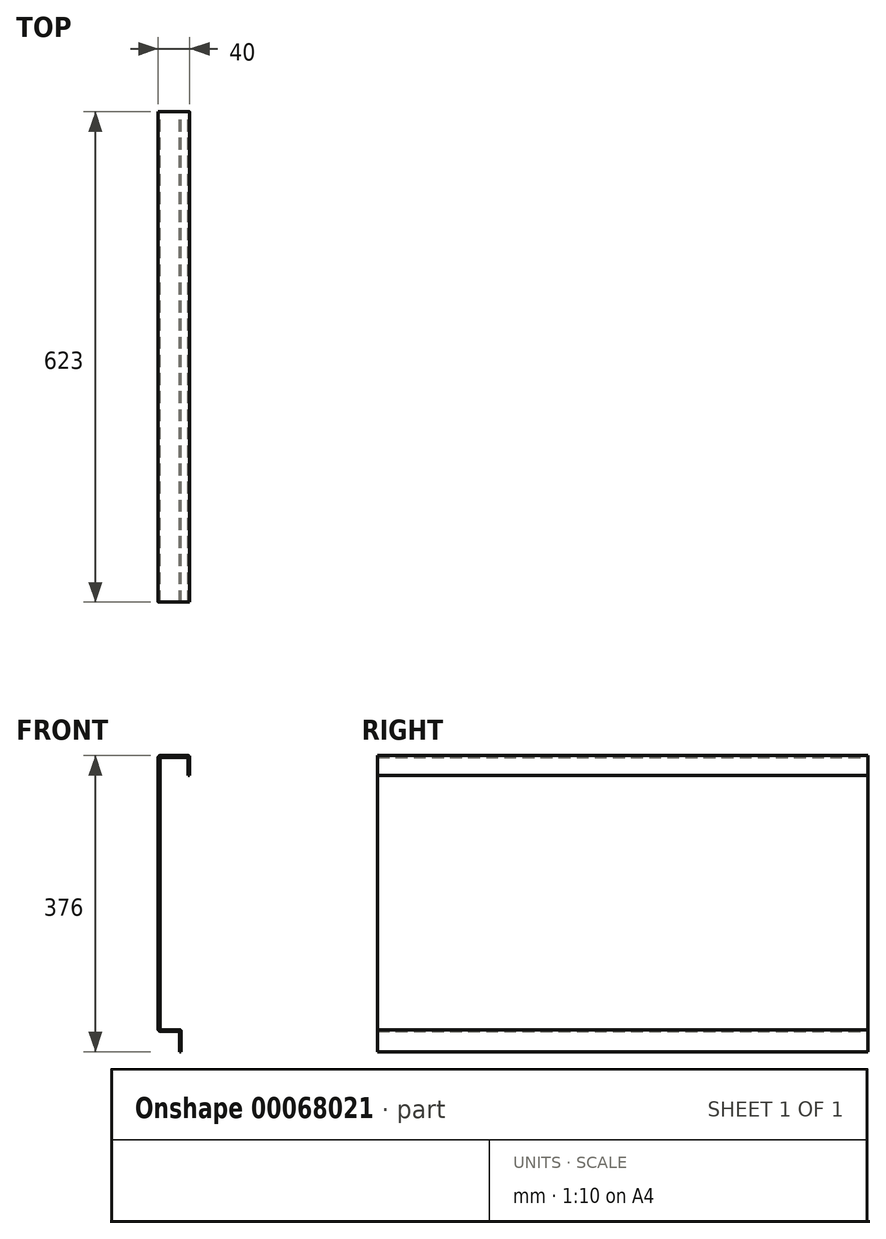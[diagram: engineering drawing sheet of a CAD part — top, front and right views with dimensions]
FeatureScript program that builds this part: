
annotation { "Feature Type Name" : "Feature", "Feature Type Description" : "" }
export const myFeature = defineFeature(function(context is Context, id is Id, definition is map)
    precondition{}
    {
        {
            var Q0;
            Q0=qCreatedBy(makeId("Front.planeOp"),FACE);
            var sketch = newSketch(context, id + "F0", { "sketchPlane" : qUnion([Q0])});
            skLineSegment(sketch, "E0", {"start": v(0, 0) * mm, "end": v(0, -350) * mm});
            skLineSegment(sketch, "E1", {"start": v(0, -350) * mm, "end": v(27, -350) * mm});
            skLineSegment(sketch, "E2", {"start": v(27, -350) * mm, "end": v(27, -376) * mm});
            skLineSegment(sketch, "E3", {"start": v(0, 0) * mm, "end": v(40, 0) * mm});
            skLineSegment(sketch, "E4", {"start": v(40, 0) * mm, "end": v(40, -25) * mm});
            skLineSegment(sketch, "E5.0", {"start": v(38, -2) * mm, "end": v(38, -25) * mm});
            skLineSegment(sketch, "E5.1", {"start": v(29, -348) * mm, "end": v(29, -376) * mm});
            skLineSegment(sketch, "E5.2", {"start": v(2, -348) * mm, "end": v(29, -348) * mm});
            skLineSegment(sketch, "E5.3", {"start": v(2, -2) * mm, "end": v(2, -348) * mm});
            skLineSegment(sketch, "E5.4", {"start": v(2, -2) * mm, "end": v(38, -2) * mm});
            skLineSegment(sketch, "E6", {"start": v(38, -25) * mm, "end": v(40, -25) * mm});
            skLineSegment(sketch, "E7", {"start": v(27, -376) * mm, "end": v(29, -376) * mm});
            skSolve(sketch);
        }
        {
            var Q0;
            Q0=qCreatedBy(makeId("Top.planeOp"),FACE);
            var sketch = newSketch(context, id + "F1", { "sketchPlane" : qUnion([Q0])});
            skLineSegment(sketch, "E8", {"start": v(0, 0) * mm, "end": v(0, 623) * mm});
            skSolve(sketch);
        }
        {
            var Q0;
            Q0=qSketchRegion(id+"F0",true);
            var Q1;
            Q1=qConstructionFilter(qBodyType(qCreatedBy(id+"F1",EDGE),BodyType.WIRE),ConstructionObject.NO);
            sweep(context, id + "F2", {"profiles" : qUnion([Q0]), "path" : qUnion([Q1])});
        }
        {
            var Q0;
            Q0=makeQuery(id+"F2.opSweep","SWEPT_EDGE",EDGE,{"disambiguationData":[OSD([sQuery(id+"F0.wireOp",EDGE,"E3"),sQuery(id+"F0.wireOp",EDGE,"E4"),sQuery(id+"F1.wireOp",EDGE,"E8")])]});
            var Q1;
            Q1=makeQuery(id+"F2.opSweep","SWEPT_EDGE",EDGE,{"disambiguationData":[OSD([sQuery(id+"F0.wireOp",EDGE,"E0"),sQuery(id+"F0.wireOp",EDGE,"E3"),sQuery(id+"F1.wireOp",EDGE,"E8")])]});
            var Q2;
            Q2=makeQuery(id+"F2.opSweep","SWEPT_EDGE",EDGE,{"disambiguationData":[OSD([sQuery(id+"F0.wireOp",EDGE,"E5.1"),sQuery(id+"F0.wireOp",EDGE,"E5.2"),sQuery(id+"F1.wireOp",EDGE,"E8")])]});
            var Q3;
            Q3=makeQuery(id+"F2.opSweep","SWEPT_EDGE",EDGE,{"disambiguationData":[OSD([sQuery(id+"F0.wireOp",EDGE,"E5.2"),sQuery(id+"F0.wireOp",EDGE,"E5.3"),sQuery(id+"F1.wireOp",EDGE,"E8")])]});
            var Q4;
            Q4=makeQuery(id+"F2.opSweep","SWEPT_EDGE",EDGE,{"disambiguationData":[OSD([sQuery(id+"F0.wireOp",EDGE,"E5.3"),sQuery(id+"F0.wireOp",EDGE,"E5.4"),sQuery(id+"F1.wireOp",EDGE,"E8")])]});
            var Q5;
            Q5=makeQuery(id+"F2.opSweep","SWEPT_EDGE",EDGE,{"disambiguationData":[OSD([sQuery(id+"F0.wireOp",EDGE,"E5.0"),sQuery(id+"F0.wireOp",EDGE,"E5.4"),sQuery(id+"F1.wireOp",EDGE,"E8")])]});
            var Q6;
            Q6=makeQuery(id+"F2.opSweep","SWEPT_EDGE",EDGE,{"disambiguationData":[OSD([sQuery(id+"F0.wireOp",EDGE,"E1"),sQuery(id+"F0.wireOp",EDGE,"E2"),sQuery(id+"F1.wireOp",EDGE,"E8")])]});
            var Q7;
            Q7=makeQuery(id+"F2.opSweep","SWEPT_EDGE",EDGE,{"disambiguationData":[OSD([sQuery(id+"F0.wireOp",EDGE,"E0"),sQuery(id+"F0.wireOp",EDGE,"E1"),sQuery(id+"F1.wireOp",EDGE,"E8")])]});
            fillet(context, id + "F3", {"entities" : qUnion([Q0, Q1, Q2, Q3, Q4, Q5, Q6, Q7]), "radius" : 2 * mm, "tangentPropagation" : true, "allowEdgeOverflow" : false});
        }
    });
